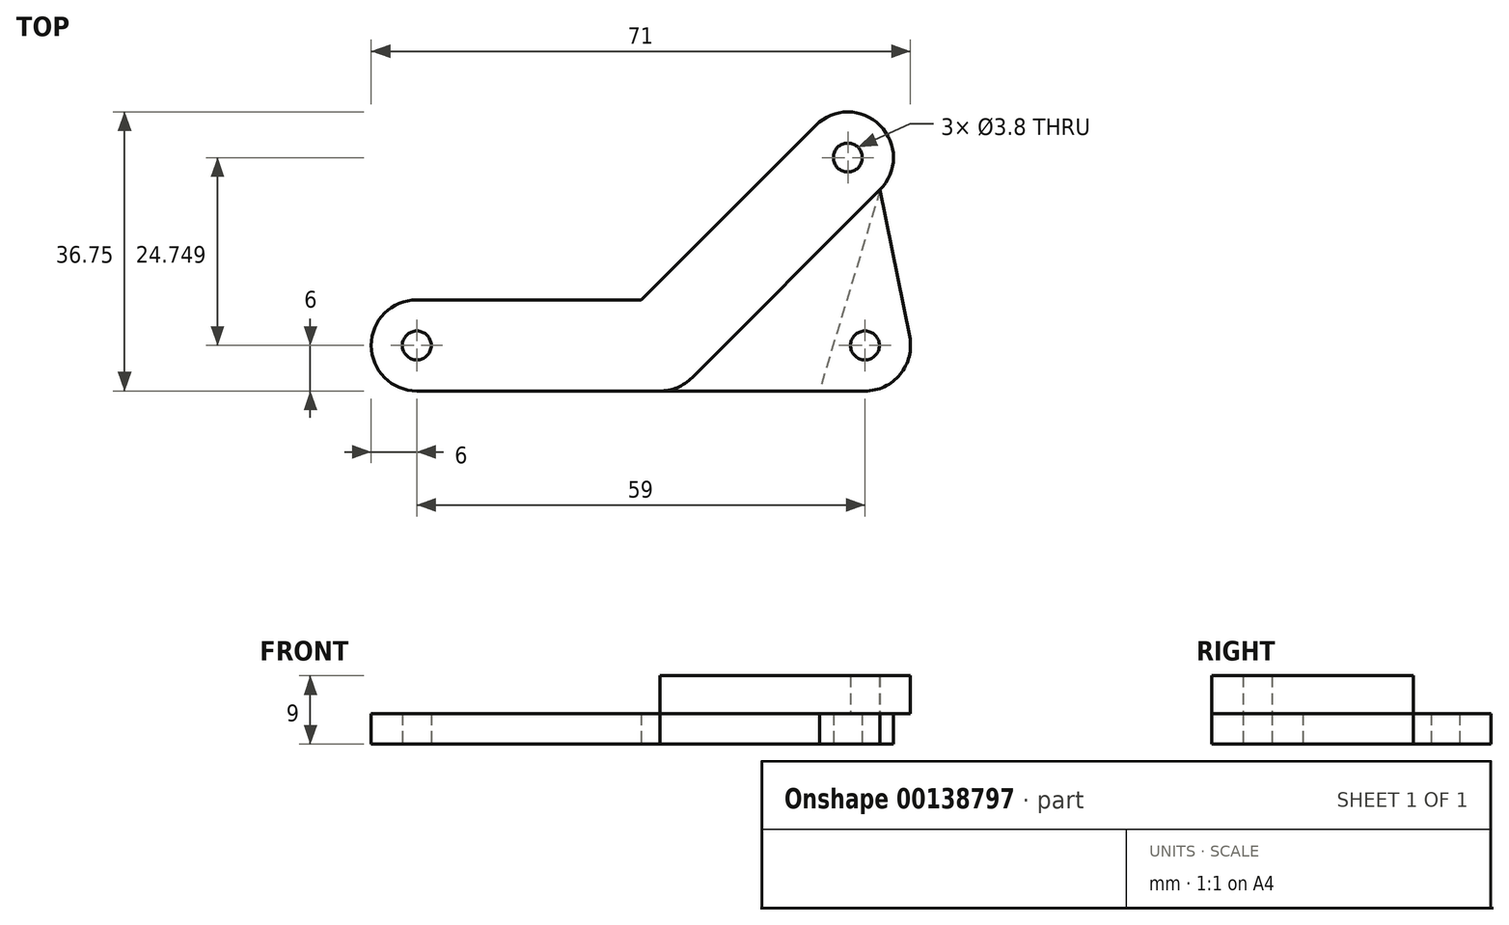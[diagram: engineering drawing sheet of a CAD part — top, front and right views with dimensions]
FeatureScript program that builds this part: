
annotation { "Feature Type Name" : "Feature", "Feature Type Description" : "" }
export const myFeature = defineFeature(function(context is Context, id is Id, definition is map)
    precondition{}
    {
        {
            var Q0;
            Q0=qCreatedBy(makeId("Top.planeOp"),FACE);
            var sketch = newSketch(context, id + "F0", { "sketchPlane" : qUnion([Q0])});
            skLineSegment(sketch, "E0", {"start": v(0, 0) * mm, "end": v(-32, 0) * mm});
            skCircle(sketch, "E1", {"center": v(-32, 0) * mm, "radius": 6 * mm});
            skLineSegment(sketch, "E2", {"start": v(0, 0) * mm, "end": v(24.75, 24.75) * mm});
            skCircle(sketch, "E3", {"center": v(24.75, 24.75) * mm, "radius": 6 * mm});
            skLineSegment(sketch, "E4", {"start": v(-32, 6) * mm, "end": v(0, 6) * mm});
            skLineSegment(sketch, "E5", {"start": v(-32, -6) * mm, "end": v(0, -6) * mm});
            skLineSegment(sketch, "E6", {"start": v(20.5, 29) * mm, "end": v(-4.24, 4.24) * mm});
            skLineSegment(sketch, "E7", {"start": v(4.24, -4.24) * mm, "end": v(29, 20.5) * mm});
            skCircle(sketch, "E8", {"center": v(-32, 0) * mm, "radius": 1.9 * mm});
            skCircle(sketch, "E9", {"center": v(24.75, 24.75) * mm, "radius": 1.9 * mm});
            skArc(sketch, "E10", {"start": v(0, -6) * mm, "mid": v(2.3, -5.54) * mm, "end": v(4.24, -4.24) * mm});
            skArc(sketch, "E11", {"start": v(4.24, -4.24) * mm, "mid": v(-2.3, 5.54) * mm, "end": v(0, -6) * mm, "construction": true});
            skSolve(sketch);
        }
        {
            var Q0;
            Q0=qSketchRegion(id+"F0",true);
            extrude(context, id + "F1", {"entities" : qUnion([Q0]), "depth" : 4 * mm});
        }
        {
            var Q0;
            Q0=makeQuery(id+"F1.opExtrude","CAP_FACE",FACE,{"disambiguationData":[OSD([sQuery(id+"F0.wireOp",EDGE,"E1"),sQuery(id+"F0.wireOp",EDGE,"E3"),sQuery(id+"F0.wireOp",EDGE,"E4"),sQuery(id+"F0.wireOp",EDGE,"E5"),sQuery(id+"F0.wireOp",EDGE,"E6"),sQuery(id+"F0.wireOp",EDGE,"E7"),sQuery(id+"F0.wireOp",EDGE,"E8"),sQuery(id+"F0.wireOp",EDGE,"E9"),sQuery(id+"F0.wireOp",EDGE,"E10")])],"isStart":false});
            var sketch = newSketch(context, id + "F2", { "sketchPlane" : qUnion([Q0])});
            skLineSegment(sketch, "E12", {"start": v(0, 0) * mm, "end": v(27, 0) * mm, "construction": true});
            skLineSegment(sketch, "E13.0", {"start": v(4.24, -4.24) * mm, "end": v(29, 20.5) * mm});
            skLineSegment(sketch, "E14", {"start": v(29, 20.5) * mm, "end": v(32.88, 1.18) * mm});
            skArc(sketch, "E15.0", {"start": v(0, -6) * mm, "mid": v(2.3, -5.54) * mm, "end": v(4.24, -4.24) * mm});
            skLineSegment(sketch, "E16", {"start": v(0, -6) * mm, "end": v(27, -6) * mm});
            skCircle(sketch, "E17", {"center": v(27, 0) * mm, "radius": 1.9 * mm});
            skArc(sketch, "E18", {"start": v(32.88, 1.18) * mm, "mid": v(22.36, 3.8) * mm, "end": v(27, -6) * mm, "construction": true});
            skArc(sketch, "E19", {"start": v(27, -6) * mm, "mid": v(31.64, -3.8) * mm, "end": v(32.88, 1.18) * mm});
            skSolve(sketch);
        }
        {
            var Q0;
            Q0=qSketchRegion(id+"F2",true);
            extrude(context, id + "F3", {"entities" : qUnion([Q0]), "depth" : 5 * mm});
        }
        {
            var Q0;
            Q0=makeQuery(id+"F3.opExtrude","CAP_FACE",FACE,{"disambiguationData":[OSD([sQuery(id+"F2.wireOp",EDGE,"E13.0"),sQuery(id+"F2.wireOp",EDGE,"E14"),sQuery(id+"F2.wireOp",EDGE,"E15.0"),sQuery(id+"F2.wireOp",EDGE,"E16"),sQuery(id+"F2.wireOp",EDGE,"E17"),sQuery(id+"F2.wireOp",EDGE,"E19")])],"isStart":true});
            var sketch = newSketch(context, id + "F4", { "sketchPlane" : qUnion([Q0])});
            skLineSegment(sketch, "E20.0", {"start": v(4.24, 4.24) * mm, "end": v(29, -20.5) * mm});
            skArc(sketch, "E21.0", {"start": v(0, 6) * mm, "mid": v(2.3, 5.54) * mm, "end": v(4.24, 4.24) * mm});
            skLineSegment(sketch, "E22.0", {"start": v(0, 6) * mm, "end": v(21, 6) * mm});
            skLineSegment(sketch, "E23", {"start": v(29, -20.5) * mm, "end": v(21, 6) * mm});
            skSolve(sketch);
        }
        {
            var Q0;
            Q0=qSketchRegion(id+"F4",true);
            extrude(context, id + "F5", {"entities" : qUnion([Q0]), "depth" : 4 * mm});
        }
    });
